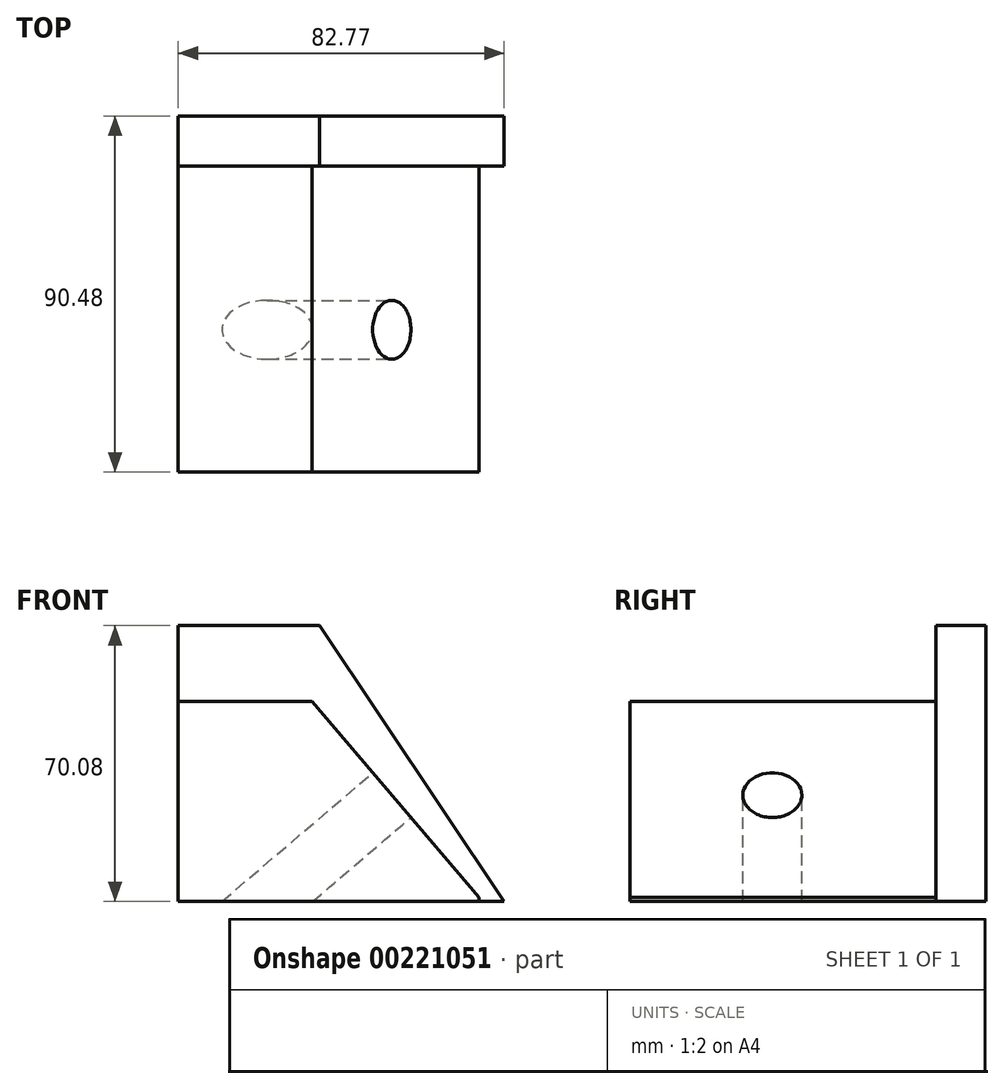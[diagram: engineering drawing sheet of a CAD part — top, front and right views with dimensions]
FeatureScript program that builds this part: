
annotation { "Feature Type Name" : "Feature", "Feature Type Description" : "" }
export const myFeature = defineFeature(function(context is Context, id is Id, definition is map)
    precondition{}
    {
        {
            var Q0;
            Q0=qCreatedBy(makeId("Top.planeOp"),FACE);
            var sketch = newSketch(context, id + "F0", { "sketchPlane" : qUnion([Q0])});
            skLineSegment(sketch, "E0.bottom", {"start": v(0, 0) * mm, "end": v(-76.44, 0) * mm});
            skLineSegment(sketch, "E0.top", {"start": v(0, -77.78) * mm, "end": v(-76.44, -77.78) * mm});
            skLineSegment(sketch, "E0.left", {"start": v(0, 0) * mm, "end": v(0, -77.78) * mm});
            skLineSegment(sketch, "E0.right", {"start": v(-76.44, 0) * mm, "end": v(-76.44, -77.78) * mm});
            skSolve(sketch);
        }
        {
            var Q0;
            Q0 = qSketchRegion(id + "F0", true);
            extrude(context, id + "F1", {"entities" : qUnion([Q0]), "depth" : 50.8 * mm});
        }
        {
            var Q0;
            Q0=makeQuery(id+"F1.opExtrude","SWEPT_FACE",FACE,{"disambiguationData":[OSD([sQuery(id+"F0.wireOp",EDGE,"E0.top")])]});
            var sketch = newSketch(context, id + "F2", { "sketchPlane" : qUnion([Q0])});
            skLineSegment(sketch, "E1", {"start": v(15.45, 50.8) * mm, "end": v(-42.48, 50.8) * mm});
            skLineSegment(sketch, "E2", {"start": v(-42.48, 50.8) * mm, "end": v(15.45, -17.05) * mm});
            skLineSegment(sketch, "E3", {"start": v(15.45, -17.05) * mm, "end": v(15.45, 50.8) * mm});
            skSolve(sketch);
        }
        {
            var Q0;
            Q0 = qSketchRegion(id + "F2", true);
            extrude(context, id + "F3", {"entities" : qUnion([Q0]), "operationType" : NewBodyOperationType.REMOVE, "endBound" : BoundingType.THROUGH_ALL, "oppositeDirection" : true, "depth" : 25.4 * mm});
        }
        {
            var Q0;
            Q0=makeQuery(id+"F3.boolean.opBoolean","COPY",FACE,{"derivedFrom":makeQuery(id+"F3.opExtrude","SWEPT_FACE",FACE,{"disambiguationData":[OSD([sQuery(id+"F2.wireOp",EDGE,"E2")])]})});
            var sketch = newSketch(context, id + "F4", { "sketchPlane" : qUnion([Q0])});
            skCircle(sketch, "E4", {"center": v(-41.6, 34.93) * mm, "radius": 7.48 * mm});
            skSolve(sketch);
        }
        {
            var Q0;
            Q0 = qSketchRegion(id + "F4", true);
            extrude(context, id + "F5", {"entities" : qUnion([Q0]), "operationType" : NewBodyOperationType.REMOVE, "endBound" : BoundingType.THROUGH_ALL, "oppositeDirection" : true, "depth" : 25.4 * mm});
        }
        {
            var Q0;
            Q0=makeQuery(id+"F1.opExtrude","SWEPT_FACE",FACE,{"disambiguationData":[OSD([sQuery(id+"F0.wireOp",EDGE,"E0.bottom")])]});
            var sketch = newSketch(context, id + "F6", { "sketchPlane" : qUnion([Q0])});
            skLineSegment(sketch, "E5.bottom", {"start": v(-6.33, 70.08) * mm, "end": v(76.44, 70.08) * mm});
            skLineSegment(sketch, "E5.top", {"start": v(-6.33, 0) * mm, "end": v(76.44, 0) * mm});
            skLineSegment(sketch, "E5.left", {"start": v(-6.33, 70.08) * mm, "end": v(-6.33, 0) * mm});
            skLineSegment(sketch, "E5.right", {"start": v(76.44, 70.08) * mm, "end": v(76.44, 0) * mm});
            skSolve(sketch);
        }
        {
            var Q0;
            Q0 = qSketchRegion(id + "F6", true);
            extrude(context, id + "F7", {"entities" : qUnion([Q0]), "operationType" : NewBodyOperationType.ADD, "depth" : 12.7 * mm});
        }
        {
            var Q0;
            Q0=makeQuery(id+"F7.opExtrude","CAP_FACE",FACE,{"disambiguationData":[OSD([sQuery(id+"F6.wireOp",EDGE,"E5.bottom"),sQuery(id+"F6.wireOp",EDGE,"E5.top"),sQuery(id+"F6.wireOp",EDGE,"E5.left"),sQuery(id+"F6.wireOp",EDGE,"E5.right")])],"isStart":false});
            var sketch = newSketch(context, id + "F8", { "sketchPlane" : qUnion([Q0])});
            skLineSegment(sketch, "E6", {"start": v(-6.33, 70.08) * mm, "end": v(40.46, 70.08) * mm});
            skLineSegment(sketch, "E7", {"start": v(40.46, 70.08) * mm, "end": v(-6.33, 35.04) * mm});
            skLineSegment(sketch, "E8", {"start": v(-6.33, 35.04) * mm, "end": v(-6.33, 70.08) * mm});
            skLineSegment(sketch, "E9", {"start": v(-6.33, 35.04) * mm, "end": v(-6.33, 0) * mm});
            skLineSegment(sketch, "E10", {"start": v(-6.33, 0) * mm, "end": v(-6.33, 35.04) * mm});
            skLineSegment(sketch, "E11", {"start": v(-6.33, 0) * mm, "end": v(40.46, 70.08) * mm});
            skSolve(sketch);
        }
        {
            var Q0;
            Q0 = qSketchRegion(id + "F8", true);
            extrude(context, id + "F9", {"entities" : qUnion([Q0]), "operationType" : NewBodyOperationType.REMOVE, "endBound" : BoundingType.THROUGH_ALL, "oppositeDirection" : true, "depth" : 25.4 * mm});
        }
    });
